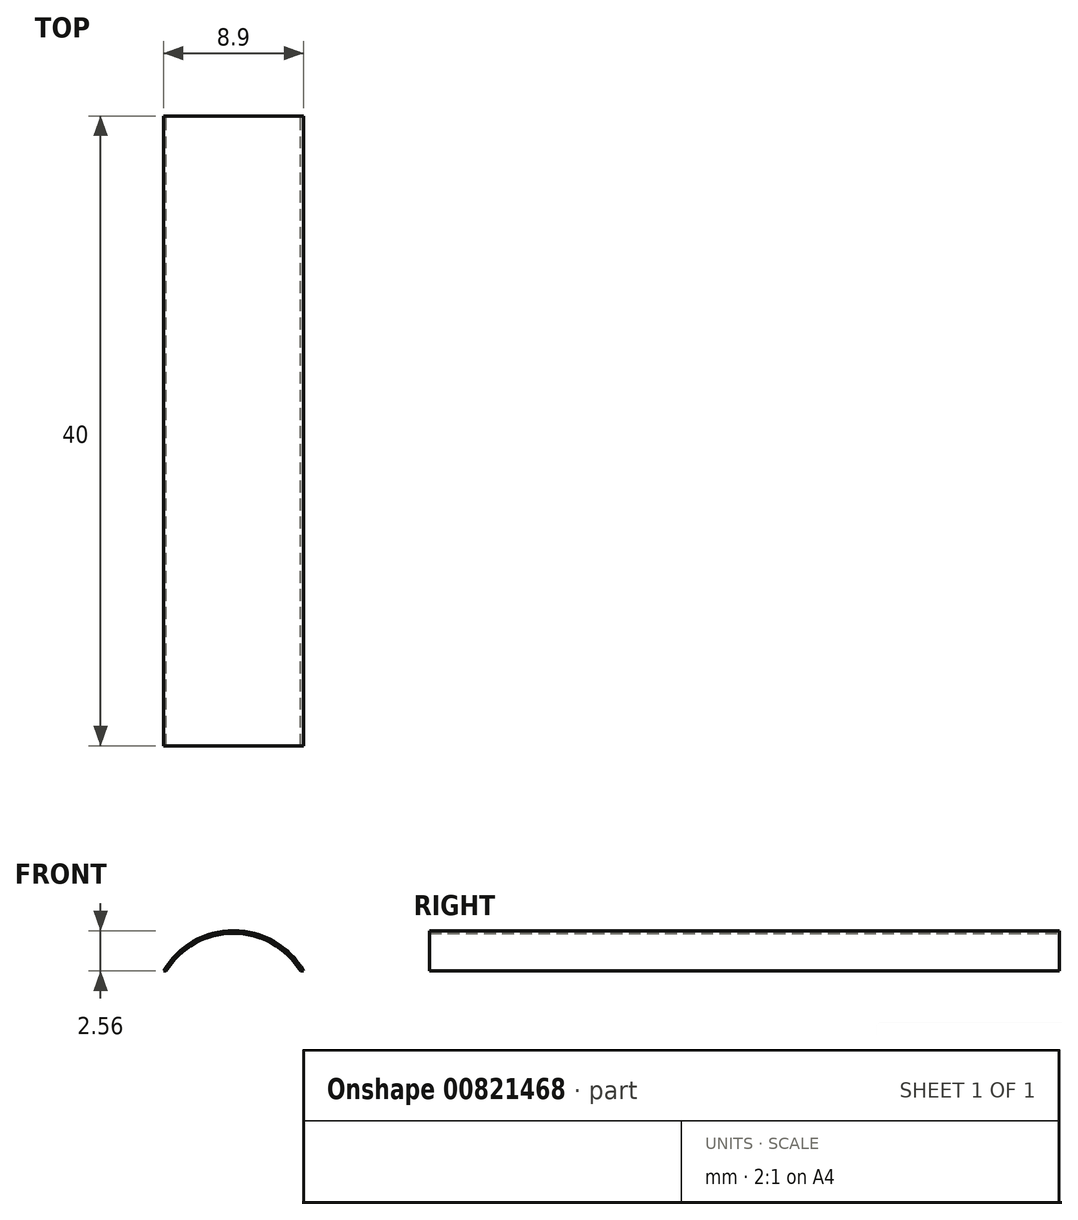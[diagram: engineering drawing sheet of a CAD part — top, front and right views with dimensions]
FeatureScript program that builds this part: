
annotation { "Feature Type Name" : "Feature", "Feature Type Description" : "" }
export const myFeature = defineFeature(function(context is Context, id is Id, definition is map)
    precondition{}
    {
        {
            var Q0;
            Q0=qCreatedBy(makeId("Front.planeOp"),FACE);
            var sketch = newSketch(context, id + "F0", { "sketchPlane" : qUnion([Q0])});
            skArc(sketch, "E0", {"start": v(4.83, 0) * mm, "mid": v(0.55, 2.4) * mm, "end": v(-3.72, 0) * mm});
            skArc(sketch, "E1", {"start": v(5.02, 0) * mm, "mid": v(0.57, 2.56) * mm, "end": v(-3.88, 0) * mm});
            skLineSegment(sketch, "E2", {"start": v(-3.88, 0) * mm, "end": v(-3.72, 0) * mm});
            skLineSegment(sketch, "E3", {"start": v(4.83, 0) * mm, "end": v(5.02, 0) * mm});
            skSolve(sketch);
        }
        {
            var Q0;
            Q0=makeQuery(id+"F0.imprint","IMPRINT",FACE,{"disambiguationData":[TD([[makeQuery(id+"F0.imprint","IMPRINT",EDGE,{"derivedFrom":sQuery(id+"F0.wireOp",EDGE,"E0")}),-1.0]])]});
            extrude(context, id + "F1", {"entities" : qUnion([Q0]), "depth" : 40 * mm, "offsetDistance" : 25.4 * mm});
        }
    });
